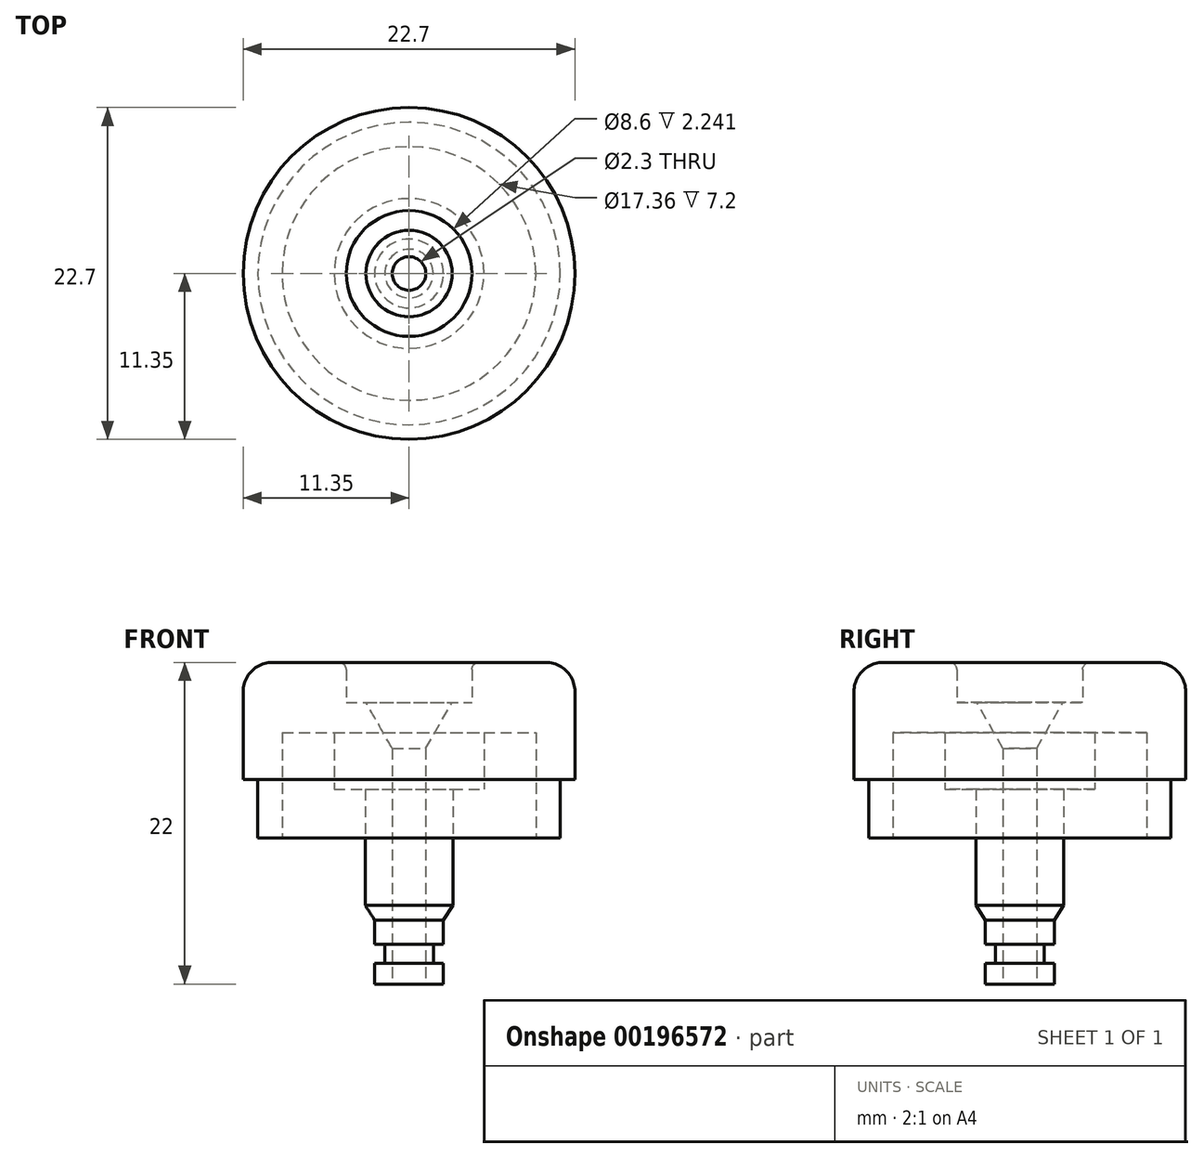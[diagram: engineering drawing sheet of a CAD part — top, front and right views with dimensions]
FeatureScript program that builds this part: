
annotation { "Feature Type Name" : "Feature", "Feature Type Description" : "" }
export const myFeature = defineFeature(function(context is Context, id is Id, definition is map)
    precondition{}
    {
        {
            var Q0;
            Q0=qCreatedBy(makeId("Front.planeOp"),FACE);
            var sketch = newSketch(context, id + "F0", { "sketchPlane" : qUnion([Q0])});
            skLineSegment(sketch, "E0", {"start": v(0, 0) * mm, "end": v(0, 22) * mm, "construction": true});
            skLineSegment(sketch, "E1", {"start": v(4.8, 22) * mm, "end": v(9.35, 22) * mm});
            skLineSegment(sketch, "E2", {"start": v(11.35, 20) * mm, "end": v(11.35, 14) * mm});
            skLineSegment(sketch, "E3", {"start": v(11.35, 14) * mm, "end": v(10.35, 14) * mm});
            skLineSegment(sketch, "E4", {"start": v(10.35, 14) * mm, "end": v(10.35, 10) * mm});
            skLineSegment(sketch, "E5", {"start": v(10.35, 10) * mm, "end": v(8.68, 10) * mm});
            skLineSegment(sketch, "E6", {"start": v(8.68, 10) * mm, "end": v(8.68, 17.2) * mm});
            skLineSegment(sketch, "E7", {"start": v(8.68, 17.2) * mm, "end": v(5.12, 17.2) * mm});
            skLineSegment(sketch, "E8", {"start": v(5.12, 17.2) * mm, "end": v(5.12, 13.31) * mm});
            skLineSegment(sketch, "E9", {"start": v(5.12, 13.31) * mm, "end": v(3, 13.31) * mm});
            skLineSegment(sketch, "E10", {"start": v(3, 13.31) * mm, "end": v(3, 5.39) * mm});
            skLineSegment(sketch, "E11", {"start": v(3, 5.39) * mm, "end": v(2.35, 4.37) * mm});
            skLineSegment(sketch, "E12", {"start": v(2.35, 4.37) * mm, "end": v(2.35, 2.7) * mm});
            skLineSegment(sketch, "E13", {"start": v(2.35, 2.7) * mm, "end": v(1.66, 2.7) * mm});
            skLineSegment(sketch, "E14", {"start": v(1.66, 2.7) * mm, "end": v(1.66, 1.41) * mm});
            skLineSegment(sketch, "E15", {"start": v(1.66, 1.41) * mm, "end": v(2.35, 1.41) * mm});
            skLineSegment(sketch, "E16", {"start": v(2.35, 1.41) * mm, "end": v(2.35, 0) * mm});
            skLineSegment(sketch, "E17", {"start": v(2.35, 0) * mm, "end": v(1.15, 0) * mm});
            skLineSegment(sketch, "E18", {"start": v(4.3, 21.5) * mm, "end": v(4.3, 19.26) * mm});
            skLineSegment(sketch, "E19", {"start": v(1.15, 16.1) * mm, "end": v(1.15, 0) * mm});
            skLineSegment(sketch, "E20", {"start": v(4.3, 19.26) * mm, "end": v(2.95, 19.26) * mm});
            skLineSegment(sketch, "E21", {"start": v(2.95, 19.26) * mm, "end": v(1.15, 16.1) * mm});
            skPoint(sketch, "E22.visualSharp", {"position": v(11.35, 22) * mm});
            skArc(sketch, "E22.filletArc", {"start": v(11.35, 20) * mm, "mid": v(10.76, 21.41) * mm, "end": v(9.35, 22) * mm});
            skPoint(sketch, "E23.visualSharp", {"position": v(4.3, 22) * mm});
            skArc(sketch, "E23.filletArc", {"start": v(4.8, 22) * mm, "mid": v(4.45, 21.85) * mm, "end": v(4.3, 21.5) * mm});
            skSolve(sketch);
        }
        {
            var Q0;
            Q0 = qSketchRegion(id + "F0", true);
            var Q1;
            Q1=sQuery(id+"F0.wireOp",EDGE,"E0");
            revolve(context, id + "F1", {"entities" : qUnion([Q0]), "axis" : qUnion([Q1]), "revolveType" : RevolveType.FULL});
        }
    });
